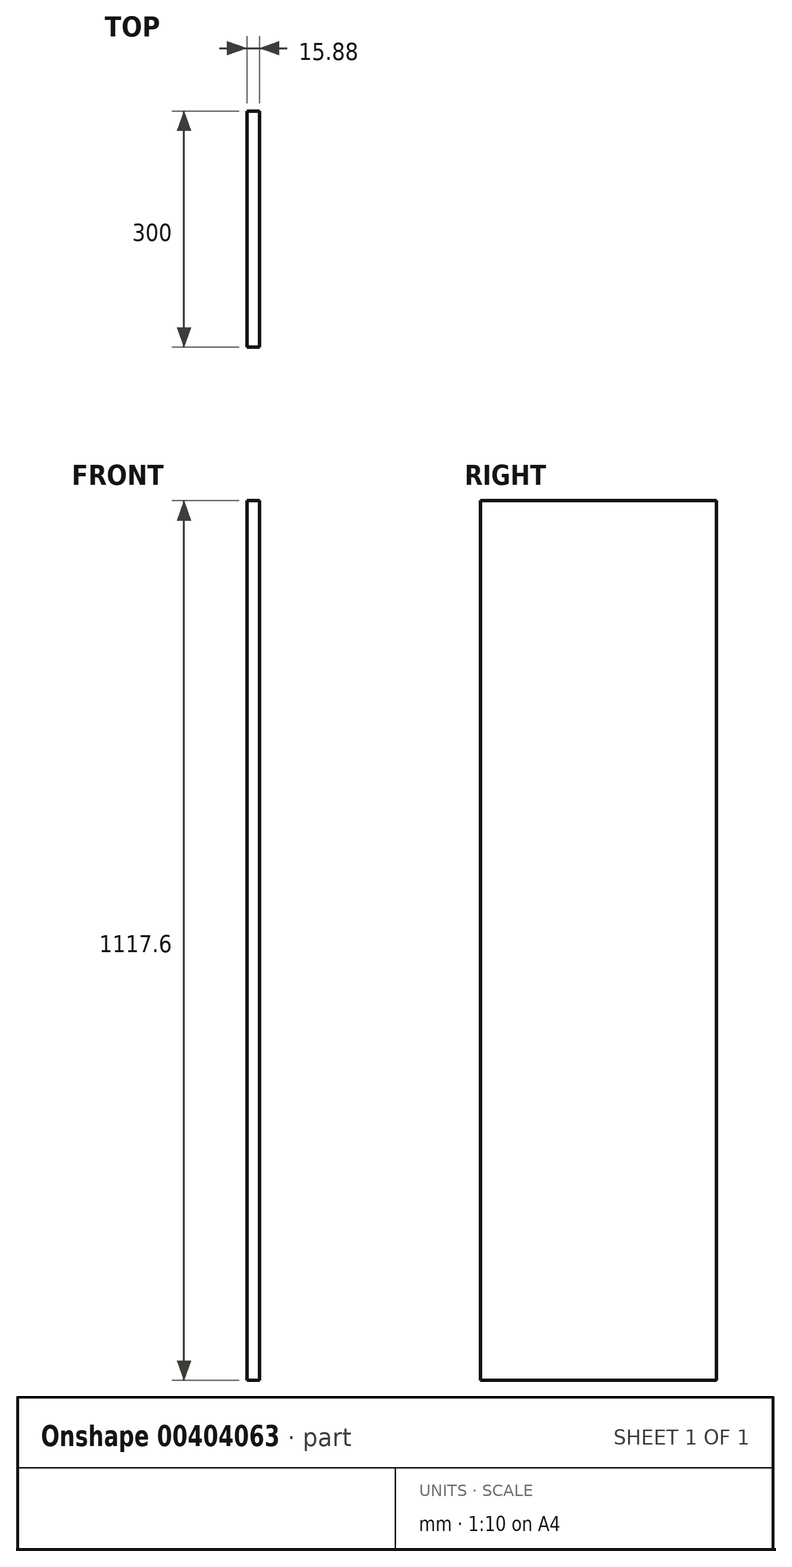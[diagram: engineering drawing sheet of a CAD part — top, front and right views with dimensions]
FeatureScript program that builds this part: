
annotation { "Feature Type Name" : "Feature", "Feature Type Description" : "" }
export const myFeature = defineFeature(function(context is Context, id is Id, definition is map)
    precondition{}
    {
        {
            var Q0;
            Q0=qCreatedBy(makeId("Right.planeOp"),FACE);
            var sketch = newSketch(context, id + "F0", { "sketchPlane" : qUnion([Q0])});
            skLineSegment(sketch, "E0.bottom", {"start": v(-153.05, 746.5) * mm, "end": v(146.95, 746.5) * mm});
            skLineSegment(sketch, "E0.top", {"start": v(-153.05, -371.1) * mm, "end": v(146.95, -371.1) * mm});
            skLineSegment(sketch, "E0.left", {"start": v(-153.05, 746.5) * mm, "end": v(-153.05, -371.1) * mm});
            skLineSegment(sketch, "E0.right", {"start": v(146.95, 746.5) * mm, "end": v(146.95, -371.1) * mm});
            skSolve(sketch);
        }
        {
            var Q0;
            Q0 = qSketchRegion(id + "F0", true);
            extrude(context, id + "F1", {"entities" : qUnion([Q0]), "depth" : 15.88 * mm});
        }
    });
